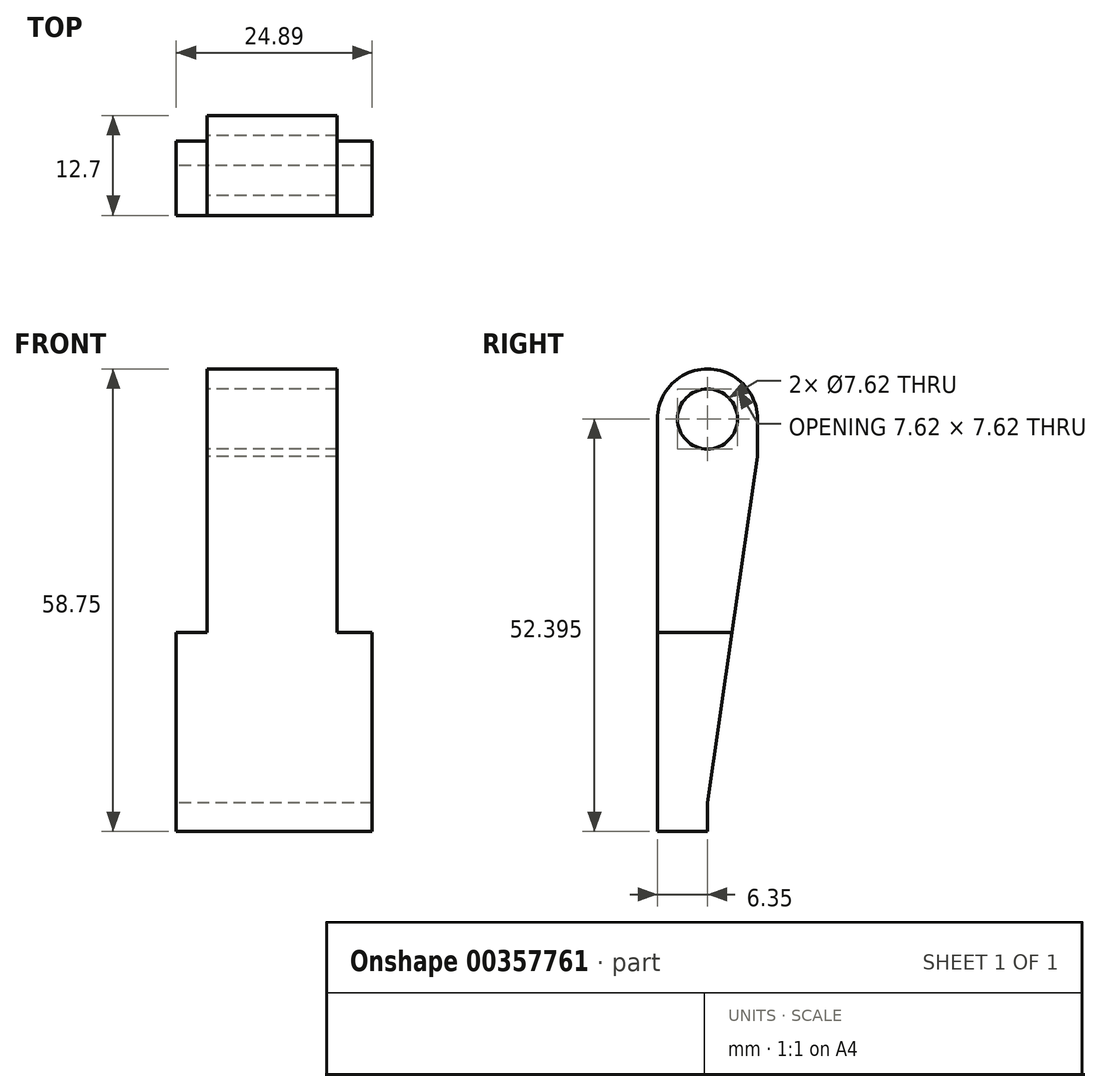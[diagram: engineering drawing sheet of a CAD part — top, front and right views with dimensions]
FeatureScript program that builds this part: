
annotation { "Feature Type Name" : "Feature", "Feature Type Description" : "" }
export const myFeature = defineFeature(function(context is Context, id is Id, definition is map)
    precondition{}
    {
        {
            var Q0;
            Q0=qCreatedBy(makeId("Front.planeOp"),FACE);
            var sketch = newSketch(context, id + "F0", { "sketchPlane" : qUnion([Q0])});
            skLineSegment(sketch, "E0.top", {"start": v(-12.7, -28.58) * mm, "end": v(12.7, -28.58) * mm});
            skLineSegment(sketch, "E0.left", {"start": v(-12.7, -3.17) * mm, "end": v(-12.7, -28.58) * mm});
            skLineSegment(sketch, "E0.right", {"start": v(12.7, -3.17) * mm, "end": v(12.7, -28.58) * mm});
            skPoint(sketch, "E0.middle", {"position": v(0, 0) * mm});
            skPoint(sketch, "E1.endSnap0", {"position": v(0, 28.58) * mm});
            skLineSegment(sketch, "E2", {"start": v(8.25, -3.17) * mm, "end": v(12.7, -3.17) * mm});
            skPoint(sketch, "E3.orphan", {"position": v(-12.7, 28.58) * mm});
            skPoint(sketch, "E4.orphan", {"position": v(12.7, 28.58) * mm});
            skLineSegment(sketch, "E5.top", {"start": v(-12.7, -3.17) * mm, "end": v(-8.26, -3.17) * mm});
            skLineSegment(sketch, "E6", {"start": v(-12.7, -3.17) * mm, "end": v(-12.7, 34.93) * mm});
            skLineSegment(sketch, "E7", {"start": v(-12.7, 34.93) * mm, "end": v(-8.25, 34.93) * mm});
            skLineSegment(sketch, "E8.MirrorCS", {"start": v(12.7, 34.93) * mm, "end": v(8.25, 34.93) * mm});
            skLineSegment(sketch, "E9.MirrorCS", {"start": v(12.7, -3.17) * mm, "end": v(12.7, 34.93) * mm});
            skLineSegment(sketch, "E10", {"start": v(-8.26, 28.58) * mm, "end": v(-3.8, 28.58) * mm});
            skLineSegment(sketch, "E11", {"start": v(3.8, 28.58) * mm, "end": v(8.25, 28.58) * mm});
            skLineSegment(sketch, "E12.trimOffspring", {"start": v(-3.8, 28.58) * mm, "end": v(-8.26, 28.58) * mm});
            skLineSegment(sketch, "E13", {"start": v(-8.26, 28.58) * mm, "end": v(8.25, 28.58) * mm});
            skLineSegment(sketch, "E14", {"start": v(8.25, 28.58) * mm, "end": v(8.25, 34.93) * mm});
            skLineSegment(sketch, "E15", {"start": v(8.25, 34.93) * mm, "end": v(12.7, 34.93) * mm});
            skLineSegment(sketch, "E16", {"start": v(-8.26, 28.58) * mm, "end": v(-8.25, 34.93) * mm});
            skLineSegment(sketch, "E17", {"start": v(-8.25, 34.93) * mm, "end": v(-12.7, 34.93) * mm});
            skLineSegment(sketch, "E18", {"start": v(-8.26, 28.58) * mm, "end": v(-8.26, -3.17) * mm});
            skLineSegment(sketch, "E19", {"start": v(8.25, 28.58) * mm, "end": v(8.25, -3.17) * mm});
            skSolve(sketch);
        }
        {
            var Q0;
            Q0=qCreatedBy(makeId("Right.planeOp"),FACE);
            var sketch = newSketch(context, id + "F1", { "sketchPlane" : qUnion([Q0])});
            skLineSegment(sketch, "E20", {"start": v(0, -3.05) * mm, "end": v(0, -28.45) * mm});
            skLineSegment(sketch, "E21", {"start": v(0, -3.05) * mm, "end": v(0, 23.95) * mm});
            skLineSegment(sketch, "E22.left", {"start": v(0, 23.95) * mm, "end": v(0, -28.45) * mm});
            skLineSegment(sketch, "E22.right", {"start": v(12.7, 23.94) * mm, "end": v(12.7, 19.2) * mm});
            skCircle(sketch, "E23", {"center": v(6.35, 23.95) * mm, "radius": 3.81 * mm});
            skLineSegment(sketch, "E24", {"start": v(0, -28.45) * mm, "end": v(6.35, -28.45) * mm});
            skLineSegment(sketch, "E25", {"start": v(6.35, -28.45) * mm, "end": v(6.35, -24.84) * mm});
            skLineSegment(sketch, "E26", {"start": v(6.35, -24.84) * mm, "end": v(12.7, 19.2) * mm});
            skArc(sketch, "E27", {"start": v(12.7, 23.94) * mm, "mid": v(6.35, 30.3) * mm, "end": v(0, 23.95) * mm});
            skPoint(sketch, "E28.orphan", {"position": v(0, 28.7) * mm});
            skPoint(sketch, "E29.endSnap0", {"position": v(6.35, 30.3) * mm});
            skPoint(sketch, "E30.end.orphan", {"position": v(0, -24.64) * mm});
            skPoint(sketch, "E29.start.orphan", {"position": v(6.35, 30.3) * mm});
            skLineSegment(sketch, "E31", {"start": v(12.7, 19.2) * mm, "end": v(0, 19.2) * mm});
            skSolve(sketch);
        }
        {
            var Q0;
            Q0 = qSketchRegion(id + "F1", true);
            extrude(context, id + "F2", {"entities" : qUnion([Q0]), "depth" : 12.7 * mm, "hasSecondDirection" : true, "secondDirectionOppositeDirection" : true, "secondDirectionDepth" : 12.2 * mm});
        }
        {
            var Q0;
            {var subQ3=sQuery(id+"F0.wireOp",EDGE,"E5.top");Q0=makeQuery(id+"F0.imprint","IMPRINT",FACE,{"disambiguationData":[TD([[makeQuery(id+"F0.imprint","IMPRINT",EDGE,{"derivedFrom":subQ3}),1.0]])]});}
            var Q1;
            {var subQ2=sQuery(id+"F0.wireOp",EDGE,"E2");Q1=makeQuery(id+"F0.imprint","IMPRINT",FACE,{"disambiguationData":[TD([[makeQuery(id+"F0.imprint","IMPRINT",EDGE,{"derivedFrom":subQ2}),1.0]])]});}
            extrude(context, id + "F3", {"entities" : qUnion([Q0, Q1]), "operationType" : NewBodyOperationType.REMOVE, "oppositeDirection" : true, "depth" : 127 * mm});
        }
    });
